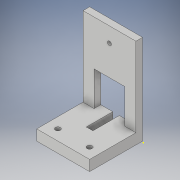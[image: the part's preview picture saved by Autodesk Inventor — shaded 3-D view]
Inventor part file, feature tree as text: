
AUTODESK INVENTOR PART (.ipt)
format: ipt  version: 2017 (Build 210142000, 142)  size: 192,000 bytes
history: native  units: in
note: dims shown in document units (in); Inventor stores cm internally (conversion verified against a paired STEP export)
features: sketch x8, extrude x7
ambient origin geometry x8: Origin, YZ Plane, XZ Plane, XY Plane, X Axis, Y Axis, Z Axis, Center Point
bodies: Solid1 (feature_tree)
feature tree (15):
  extrude  "Extrusion1"  Depth=2.0in
  extrude  "Extrusion2"  TaperAngle=0.0deg  [1 undecoded]
  extrude  "Extrusion3"  Depth=2.0in
  extrude  "Extrusion5"  Depth=1.3in
  extrude  "Extrusion6"  TaperAngle=0.0deg  [1 undecoded]
  extrude  "Extrusion7"  Depth=0.6in
  extrude  "Extrusion8"  Depth=0.57in
  sketch  "Sketch10"  dims[d20=0.25in d21=0.0in d26=0.9683in d27=1.0125in d28=0.6in d29=0.445in d30=0.15in d31=1.0in d32=0.0in d33=0.57in d34=0.25in d35=0.0in d36=0.1875in d37=0.1875in d38=0.4in d39=0.4in d40=0.4in d41=0.4in d42=1.0in d43=0.0in d45=0.25in d46=0.125in d47=1.0in d48=0.0in]
  sketch  "Sketch1"  dims[d1=0.4in d2=2.0in]
  sketch  "Sketch2"  dims[d3=2.0in d4=0.0in d6=0.0in]
  sketch  "Sketch3"  dims[d7=2.0in d9=0.58in]
  sketch  "Sketch5"  dims[d10=0.58in d11=1.3in]
  sketch  "Sketch6"  dims[d12=0.25in d13=0.0in d15=0.0in]
  sketch  "Sketch8"  dims[d16=2.025in d17=0.6in]
  sketch  "Sketch9"  dims[d18=0.0in d19=0.57in]
note: 2 required parameter values undecoded (feature->parameter linkage not recoverable at this tier; creation-order binding heuristic only, values carry confidence <= 0.55)
